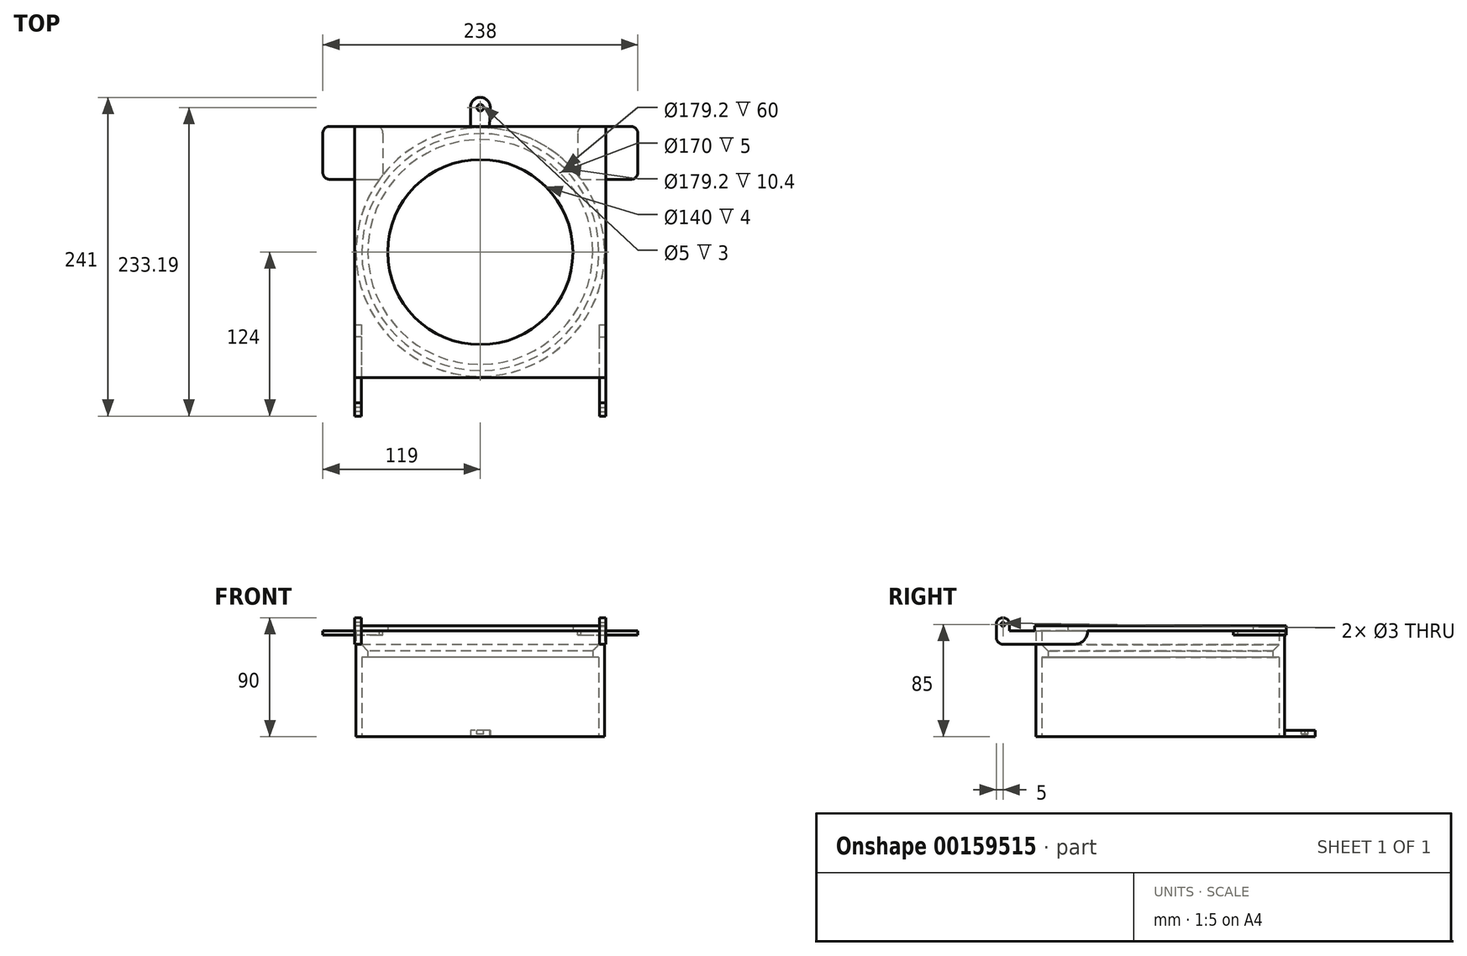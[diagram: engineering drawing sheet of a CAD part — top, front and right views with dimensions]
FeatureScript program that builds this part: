
annotation { "Feature Type Name" : "Feature", "Feature Type Description" : "" }
export const myFeature = defineFeature(function(context is Context, id is Id, definition is map)
    precondition{}
    {
        {
            var Q0;
            Q0=qCreatedBy(makeId("Top.planeOp"),FACE);
            var sketch = newSketch(context, id + "F0", { "sketchPlane" : qUnion([Q0])});
            skCircle(sketch, "E0", {"center": v(0, 0) * mm, "radius": 94 * mm});
            skCircle(sketch, "E1", {"center": v(0, 0) * mm, "radius": 89.6 * mm});
            skArc(sketch, "E2", {"start": v(7.5, 109.26) * mm, "mid": v(-0.04, 117) * mm, "end": v(-7.5, 109.19) * mm});
            skLineSegment(sketch, "E3", {"start": v(-7.5, 109.19) * mm, "end": v(-7.5, 93.7) * mm});
            skLineSegment(sketch, "E4", {"start": v(7.5, 109.26) * mm, "end": v(7, 93.74) * mm});
            skSolve(sketch);
        }
        {
            var Q0;
            Q0=makeQuery(id+"F0.imprint","IMPRINT",FACE,{"disambiguationData":[TD([[makeQuery(id+"F0.imprint","IMPRINT",EDGE,{"derivedFrom":sQuery(id+"F0.wireOp",EDGE,"E0")}),1.0]])]});
            extrude(context, id + "F1", {"entities" : qUnion([Q0]), "depth" : 60 * mm});
        }
        {
            var Q0;
            Q0=makeQuery(id+"F1.opExtrude","CAP_FACE",FACE,{"disambiguationData":[OSD([sQuery(id+"F0.wireOp",EDGE,"E0"),sQuery(id+"F0.wireOp",EDGE,"E1")])],"isStart":false});
            var sketch = newSketch(context, id + "F2", { "sketchPlane" : qUnion([Q0])});
            skCircle(sketch, "E5", {"center": v(0, 0) * mm, "radius": 94 * mm});
            skCircle(sketch, "E6", {"center": v(0, 0) * mm, "radius": 85 * mm});
            skSolve(sketch);
        }
        {
            var Q0;
            Q0=makeQuery(id+"F2.imprint","IMPRINT",FACE,{"disambiguationData":[TD([[makeQuery(id+"F2.imprint","IMPRINT",EDGE,{"derivedFrom":sQuery(id+"F2.wireOp",EDGE,"E6")}),-1.0]])]});
            var Q1;
            Q1=makeQuery(id+"F2.imprint","IMPRINT",FACE,{"disambiguationData":[TD([[makeQuery(id+"F2.imprint","IMPRINT",EDGE,{"derivedFrom":sQuery(id+"F2.wireOp",EDGE,"E5")}),1.0]])]});
            extrude(context, id + "F3", {"entities" : qUnion([Q0, Q1]), "operationType" : NewBodyOperationType.ADD, "depth" : 10 * mm});
        }
        {
            var Q0;
            Q0=makeQuery(id+"F3.opExtrude","CAP_FACE",FACE,{"disambiguationData":[OSD([sQuery(id+"F2.wireOp",EDGE,"E5"),sQuery(id+"F2.wireOp",EDGE,"E6")])],"isStart":false});
            var sketch = newSketch(context, id + "F4", { "sketchPlane" : qUnion([Q0])});
            skCircle(sketch, "E7", {"center": v(0, 0) * mm, "radius": 94 * mm});
            skCircle(sketch, "E8", {"center": v(0, 0) * mm, "radius": 89.6 * mm});
            skSolve(sketch);
        }
        {
            var Q0;
            Q0=makeQuery(id+"F4.imprint","IMPRINT",FACE,{"disambiguationData":[TD([[makeQuery(id+"F4.imprint","IMPRINT",EDGE,{"derivedFrom":sQuery(id+"F4.wireOp",EDGE,"E7")}),1.0]])]});
            extrude(context, id + "F5", {"entities" : qUnion([Q0]), "operationType" : NewBodyOperationType.ADD, "depth" : 10 * mm});
        }
        {
            var Q0;
            Q0=makeQuery(id+"F5.opExtrude","CAP_FACE",FACE,{"disambiguationData":[OSD([sQuery(id+"F4.wireOp",EDGE,"E7"),sQuery(id+"F4.wireOp",EDGE,"E8")])],"isStart":false});
            var sketch = newSketch(context, id + "F6", { "sketchPlane" : qUnion([Q0])});
            skLineSegment(sketch, "E9.bottom", {"start": v(95, -95) * mm, "end": v(-95, -95) * mm});
            skLineSegment(sketch, "E9.top", {"start": v(95, 95) * mm, "end": v(-95, 95) * mm});
            skLineSegment(sketch, "E9.left", {"start": v(95, -95) * mm, "end": v(95, 95) * mm});
            skLineSegment(sketch, "E9.right", {"start": v(-95, -95) * mm, "end": v(-95, 95) * mm});
            skPoint(sketch, "E9.middle", {"position": v(0, 0) * mm});
            skCircle(sketch, "E10", {"center": v(0, 0) * mm, "radius": 70 * mm});
            skSolve(sketch);
        }
        {
            var Q0;
            Q0=makeQuery(id+"F6.imprint","IMPRINT",FACE,{"disambiguationData":[TD([[makeQuery(id+"F6.imprint","IMPRINT",EDGE,{"derivedFrom":sQuery(id+"F6.wireOp",EDGE,"E9.bottom")}),-1.0]])]});
            var Q1;
            Q1=makeQuery(id+"F6.imprint","IMPRINT",FACE,{"disambiguationData":[TD([[makeQuery(id+"F6.imprint","IMPRINT",EDGE,{"derivedFrom":sQuery(id+"F6.wireOp",EDGE,"E10")}),-1.0]])]});
            var Q2;
            Q2=makeQuery(id+"F6.imprint","IMPRINT",FACE,{"disambiguationData":[TD([[makeQuery(id+"F6.imprint","IMPRINT",EDGE,{"derivedFrom":makeQuery(id+"F5.opExtrude","CAP_EDGE",EDGE,{"disambiguationData":[OSD([sQuery(id+"F4.wireOp",EDGE,"E7")])],"isStart":false})}),1.0]])]});
            extrude(context, id + "F7", {"entities" : qUnion([Q0, Q1, Q2]), "operationType" : NewBodyOperationType.ADD, "depth" : 4 * mm});
        }
        {
            var Q0;
            Q0=makeQuery(id+"F0.imprint","IMPRINT",FACE,{"disambiguationData":[TD([[makeQuery(id+"F0.imprint","IMPRINT",EDGE,{"derivedFrom":sQuery(id+"F0.wireOp",EDGE,"E2")}),1.0]])]});
            extrude(context, id + "F8", {"entities" : qUnion([Q0]), "operationType" : NewBodyOperationType.ADD, "depth" : 5 * mm});
        }
        {
            var Q0;
            Q0=makeQuery(id+"F8.opExtrude","CAP_FACE",FACE,{"disambiguationData":[OSD([sQuery(id+"F0.wireOp",EDGE,"E0"),sQuery(id+"F0.wireOp",EDGE,"E2"),sQuery(id+"F0.wireOp",EDGE,"E3"),sQuery(id+"F0.wireOp",EDGE,"E4")])],"isStart":false});
            var sketch = newSketch(context, id + "F9", { "sketchPlane" : qUnion([Q0])});
            skCircle(sketch, "E11", {"center": v(0, 109.19) * mm, "radius": 2.5 * mm});
            skSolve(sketch);
        }
        {
            var Q0;
            Q0=makeQuery(id+"F9.imprint","IMPRINT",FACE,{"disambiguationData":[TD([[makeQuery(id+"F9.imprint","IMPRINT",EDGE,{"derivedFrom":sQuery(id+"F9.wireOp",EDGE,"E11")}),1.0]])]});
            extrude(context, id + "F10", {"entities" : qUnion([Q0]), "operationType" : NewBodyOperationType.REMOVE, "oppositeDirection" : true, "depth" : 3 * mm});
        }
        {
            var Q0;
            Q0=makeQuery(id+"F3.opExtrude","CAP_EDGE",EDGE,{"disambiguationData":[OSD([sQuery(id+"F2.wireOp",EDGE,"E6")])],"isStart":false});
            chamfer(context, id + "F11", {"entities" : qUnion([Q0]), "width" : 5 * mm, "tangentPropagation" : true});
        }
        {
            var Q0;
            {var subQ0=sQuery(id+"F6.wireOp",EDGE,"E9.bottom");var subQ1=sQuery(id+"F6.wireOp",EDGE,"E9.top");var subQ2=sQuery(id+"F6.wireOp",EDGE,"E9.left");var subQ3=sQuery(id+"F6.wireOp",EDGE,"E9.right");Q0=makeQuery(id+"F7.boolean.opBoolean","SPLIT",FACE,{"disambiguationData":[TD([makeQuery(id+"F1.opExtrude","SWEPT_FACE",FACE,{"disambiguationData":[OSD([sQuery(id+"F0.wireOp",EDGE,"E0")])]})])],"derivedFrom":makeQuery(id+"F7.opExtrude","CAP_FACE",FACE,{"disambiguationData":[OSD([subQ0,subQ1,subQ2,subQ3,sQuery(id+"F6.wireOp",EDGE,"E10")])],"isStart":true})});}
            var sketch = newSketch(context, id + "F12", { "sketchPlane" : qUnion([Q0])});
            skLineSegment(sketch, "E12.bottom", {"start": v(95, -95) * mm, "end": v(114, -95) * mm});
            skLineSegment(sketch, "E12.top", {"start": v(95, -55) * mm, "end": v(114, -55) * mm});
            skLineSegment(sketch, "E12.right", {"start": v(119, -90) * mm, "end": v(119, -60) * mm});
            skPoint(sketch, "E13.visualSharp", {"position": v(119, -95) * mm});
            skArc(sketch, "E13.filletArc", {"start": v(114, -95) * mm, "mid": v(117.54, -93.54) * mm, "end": v(119, -90) * mm});
            skPoint(sketch, "E14.visualSharp", {"position": v(119, -55) * mm});
            skArc(sketch, "E14.filletArc", {"start": v(119, -60) * mm, "mid": v(117.54, -56.46) * mm, "end": v(114, -55) * mm});
            skLineSegment(sketch, "E15.bottom", {"start": v(95, -95) * mm, "end": v(78.59, -95) * mm});
            skLineSegment(sketch, "E15.top", {"start": v(95, -55) * mm, "end": v(73.59, -55) * mm});
            skLineSegment(sketch, "E15.right", {"start": v(73.59, -90) * mm, "end": v(73.59, -55) * mm});
            skPoint(sketch, "E16.visualSharp", {"position": v(73.59, -95) * mm});
            skArc(sketch, "E16.filletArc", {"start": v(73.59, -90) * mm, "mid": v(75.05, -93.54) * mm, "end": v(78.59, -95) * mm});
            skLineSegment(sketch, "E17.MirrorCS", {"start": v(-95, -95) * mm, "end": v(-114, -95) * mm});
            skLineSegment(sketch, "E18.MirrorCS", {"start": v(-95, -95) * mm, "end": v(-78.59, -95) * mm});
            skArc(sketch, "E19.MirrorCS", {"start": v(-73.59, -90) * mm, "mid": v(-75.05, -93.54) * mm, "end": v(-78.59, -95) * mm});
            skLineSegment(sketch, "E20.MirrorCS", {"start": v(-73.59, -90) * mm, "end": v(-73.59, -55) * mm});
            skLineSegment(sketch, "E21.MirrorCS", {"start": v(-95, -55) * mm, "end": v(-73.59, -55) * mm});
            skLineSegment(sketch, "E22.MirrorCS", {"start": v(-95, -55) * mm, "end": v(-114, -55) * mm});
            skArc(sketch, "E23.MirrorCS", {"start": v(-119, -60) * mm, "mid": v(-117.54, -56.46) * mm, "end": v(-114, -55) * mm});
            skLineSegment(sketch, "E24.MirrorCS", {"start": v(-119, -90) * mm, "end": v(-119, -60) * mm});
            skArc(sketch, "E25.MirrorCS", {"start": v(-114, -95) * mm, "mid": v(-117.54, -93.54) * mm, "end": v(-119, -90) * mm});
            skSolve(sketch);
        }
        {
            var Q0;
            {var subQ1=sQuery(id+"F12.wireOp",EDGE,"E12.bottom");Q0=makeQuery(id+"F12.imprint","IMPRINT",FACE,{"disambiguationData":[TD([[makeQuery(id+"F12.imprint","IMPRINT",EDGE,{"derivedFrom":subQ1}),1.0]])]});}
            var Q1;
            {var subQ8=sQuery(id+"F12.wireOp",EDGE,"E15.bottom");Q1=makeQuery(id+"F12.imprint","IMPRINT",FACE,{"disambiguationData":[TD([[makeQuery(id+"F12.imprint","IMPRINT",EDGE,{"derivedFrom":subQ8}),-1.0]])]});}
            var Q2;
            {var subQ8=sQuery(id+"F12.wireOp",EDGE,"E18.MirrorCS");Q2=makeQuery(id+"F12.imprint","IMPRINT",FACE,{"disambiguationData":[TD([[makeQuery(id+"F12.imprint","IMPRINT",EDGE,{"derivedFrom":subQ8}),-1.0]])]});}
            var Q3;
            {var subQ1=sQuery(id+"F12.wireOp",EDGE,"E17.MirrorCS");Q3=makeQuery(id+"F12.imprint","IMPRINT",FACE,{"disambiguationData":[TD([[makeQuery(id+"F12.imprint","IMPRINT",EDGE,{"derivedFrom":subQ1}),-1.0]])]});}
            extrude(context, id + "F13", {"entities" : qUnion([Q0, Q1, Q2, Q3]), "operationType" : NewBodyOperationType.ADD, "depth" : 3 * mm});
        }
        {
            var Q0;
            {var subQ0=sQuery(id+"F6.wireOp",EDGE,"E9.bottom");var subQ1=makeQuery(id+"F7.opExtrude","SWEPT_FACE",FACE,{"disambiguationData":[OSD([subQ0])]});var subQ9=makeQuery(id+"F1.opExtrude","SWEPT_FACE",FACE,{"disambiguationData":[OSD([sQuery(id+"F0.wireOp",EDGE,"E0")])]});var subQ10=sQuery(id+"F6.wireOp",EDGE,"E9.left");var subQ12=sQuery(id+"F6.wireOp",EDGE,"E9.right");var subQ14=sQuery(id+"F6.wireOp",EDGE,"E9.top");Q0=makeQuery(id+"F13.boolean.opBoolean","SPLIT",FACE,{"disambiguationData":[TD([subQ1])],"derivedFrom":makeQuery(id+"F7.boolean.opBoolean","SPLIT",FACE,{"disambiguationData":[TD([subQ9])],"derivedFrom":makeQuery(id+"F7.opExtrude","CAP_FACE",FACE,{"disambiguationData":[OSD([subQ0,subQ14,subQ10,subQ12,sQuery(id+"F6.wireOp",EDGE,"E10")])],"isStart":true})})});}
            var sketch = newSketch(context, id + "F14", { "sketchPlane" : qUnion([Q0])});
            skLineSegment(sketch, "E26.bottom", {"start": v(-95, 95) * mm, "end": v(-90, 95) * mm});
            skLineSegment(sketch, "E26.top", {"start": v(-95, 119) * mm, "end": v(-90, 119) * mm});
            skLineSegment(sketch, "E26.left", {"start": v(-95, 95) * mm, "end": v(-95, 119) * mm});
            skLineSegment(sketch, "E26.right", {"start": v(-90, 95) * mm, "end": v(-90, 119) * mm});
            skLineSegment(sketch, "E27.top", {"start": v(-95, 55) * mm, "end": v(-90, 55) * mm});
            skLineSegment(sketch, "E27.left", {"start": v(-95, 95) * mm, "end": v(-95, 55) * mm});
            skLineSegment(sketch, "E27.right", {"start": v(-90, 95) * mm, "end": v(-90, 55) * mm});
            skLineSegment(sketch, "E28.top", {"start": v(-95, 124) * mm, "end": v(-90, 124) * mm});
            skLineSegment(sketch, "E28.left", {"start": v(-95, 119) * mm, "end": v(-95, 124) * mm});
            skLineSegment(sketch, "E28.right", {"start": v(-90, 119) * mm, "end": v(-90, 124) * mm});
            skSolve(sketch);
        }
        {
            var Q0;
            Q0 = qSketchRegion(id + "F14", true);
            extrude(context, id + "F15", {"entities" : qUnion([Q0]), "operationType" : NewBodyOperationType.ADD, "depth" : 10 * mm});
        }
        {
            var Q0;
            Q0=makeQuery(id+"F15.boolean.opBoolean","MERGE",FACE,{"derivedFrom":[makeQuery(id+"F7.opExtrude","SWEPT_FACE",FACE,{"disambiguationData":[OSD([sQuery(id+"F6.wireOp",EDGE,"E9.right")])]}),makeQuery(id+"F15.opExtrude","SWEPT_FACE",FACE,{"disambiguationData":[OSD([sQuery(id+"F14.wireOp",EDGE,"E26.left"),sQuery(id+"F14.wireOp",EDGE,"E27.left")])]})]});
            var sketch = newSketch(context, id + "F16", { "sketchPlane" : qUnion([Q0])});
            skArc(sketch, "E29", {"start": v(55, 80) * mm, "mid": v(58.27, 72.58) * mm, "end": v(65.95, 70) * mm});
            skSolve(sketch);
        }
        {
            var Q0;
            Q0 = qSketchRegion(id + "F16", true);
            var Q1;
            {var subQ3=sQuery(id+"F6.wireOp",EDGE,"E9.right");var subQ5=sQuery(id+"F14.wireOp",EDGE,"E27.left");var subQ6=makeQuery(id+"F15.opExtrude","SWEPT_EDGE",EDGE,{"disambiguationData":[OSD([subQ3,sQuery(id+"F14.wireOp",EDGE,"E27.top"),subQ5])]});Q1=makeQuery(id+"F16.imprint","IMPRINT",FACE,{"disambiguationData":[TD([[makeQuery(id+"F16.imprint","IMPRINT",EDGE,{"derivedFrom":subQ6}),-1.0]])]});}
            extrude(context, id + "F17", {"entities" : qUnion([Q0, Q1]), "operationType" : NewBodyOperationType.REMOVE, "endBound" : BoundingType.UP_TO_NEXT, "oppositeDirection" : true, "depth" : 25 * mm});
        }
        {
            var Q0;
            Q0=makeQuery(id+"F15.opExtrude","CAP_EDGE",EDGE,{"disambiguationData":[OSD([sQuery(id+"F14.wireOp",EDGE,"E28.top")])],"isStart":false});
            fillet(context, id + "F18", {"entities" : qUnion([Q0]), "radius" : 5 * mm, "tangentPropagation" : true, "allowEdgeOverflow" : false});
        }
        {
            var Q0;
            Q0=makeQuery(id+"F15.boolean.opBoolean","MERGE",FACE,{"derivedFrom":[makeQuery(id+"F7.opExtrude","SWEPT_FACE",FACE,{"disambiguationData":[OSD([sQuery(id+"F6.wireOp",EDGE,"E9.right")])]}),makeQuery(id+"F15.opExtrude","SWEPT_FACE",FACE,{"disambiguationData":[OSD([sQuery(id+"F14.wireOp",EDGE,"E26.left"),sQuery(id+"F14.wireOp",EDGE,"E27.left"),sQuery(id+"F14.wireOp",EDGE,"E28.left")])]})]});
            var sketch = newSketch(context, id + "F19", { "sketchPlane" : qUnion([Q0])});
            skLineSegment(sketch, "E30.bottom", {"start": v(124, 80) * mm, "end": v(114, 80) * mm});
            skLineSegment(sketch, "E30.top", {"start": v(119, 90) * mm, "end": v(119, 90) * mm});
            skLineSegment(sketch, "E30.left", {"start": v(124, 80) * mm, "end": v(124, 85) * mm});
            skLineSegment(sketch, "E30.right", {"start": v(114, 80) * mm, "end": v(114, 85) * mm});
            skPoint(sketch, "E31.visualSharp", {"position": v(124, 90) * mm});
            skArc(sketch, "E31.filletArc", {"start": v(124, 85) * mm, "mid": v(122.54, 88.54) * mm, "end": v(119, 90) * mm});
            skPoint(sketch, "E32.visualSharp", {"position": v(114, 90) * mm});
            skArc(sketch, "E32.filletArc", {"start": v(119, 90) * mm, "mid": v(115.46, 88.54) * mm, "end": v(114, 85) * mm});
            skSolve(sketch);
        }
        {
            var Q0;
            Q0=makeQuery(id+"F19.imprint","IMPRINT",FACE,{"disambiguationData":[TD([[makeQuery(id+"F19.imprint","IMPRINT",EDGE,{"derivedFrom":sQuery(id+"F19.wireOp",EDGE,"E30.bottom")}),1.0]])]});
            extrude(context, id + "F20", {"entities" : qUnion([Q0]), "operationType" : NewBodyOperationType.ADD, "oppositeDirection" : true, "depth" : 5 * mm});
        }
        {
            var Q0;
            Q0=makeQuery(id+"F20.boolean.opBoolean","MERGE",FACE,{"derivedFrom":[makeQuery(id+"F15.boolean.opBoolean","MERGE",FACE,{"derivedFrom":[makeQuery(id+"F7.opExtrude","SWEPT_FACE",FACE,{"disambiguationData":[OSD([sQuery(id+"F6.wireOp",EDGE,"E9.right")])]}),makeQuery(id+"F15.opExtrude","SWEPT_FACE",FACE,{"disambiguationData":[OSD([sQuery(id+"F14.wireOp",EDGE,"E26.left"),sQuery(id+"F14.wireOp",EDGE,"E27.left"),sQuery(id+"F14.wireOp",EDGE,"E28.left")])]})]}),makeQuery(id+"F20.opExtrude","CAP_FACE",FACE,{"disambiguationData":[OSD([sQuery(id+"F19.wireOp",EDGE,"E30.bottom"),sQuery(id+"F19.wireOp",EDGE,"E30.left"),sQuery(id+"F19.wireOp",EDGE,"E30.right"),sQuery(id+"F19.wireOp",EDGE,"E31.filletArc"),sQuery(id+"F19.wireOp",EDGE,"E32.filletArc")])],"isStart":true})]});
            var sketch = newSketch(context, id + "F21", { "sketchPlane" : qUnion([Q0])});
            skCircle(sketch, "E33", {"center": v(119, 85) * mm, "radius": 1.5 * mm});
            skSolve(sketch);
        }
        {
            var Q0;
            Q0=makeQuery(id+"F21.imprint","IMPRINT",FACE,{"disambiguationData":[TD([[makeQuery(id+"F21.imprint","IMPRINT",EDGE,{"derivedFrom":sQuery(id+"F21.wireOp",EDGE,"E33")}),1.0]])]});
            extrude(context, id + "F22", {"entities" : qUnion([Q0]), "operationType" : NewBodyOperationType.REMOVE, "endBound" : BoundingType.UP_TO_NEXT, "oppositeDirection" : true, "depth" : 25 * mm});
        }
        {
            var Q0;
            Q0=makeQuery(id+"F7.opExtrude","SWEPT_FACE",FACE,{"disambiguationData":[OSD([sQuery(id+"F6.wireOp",EDGE,"E9.left")])]});
            var sketch = newSketch(context, id + "F23", { "sketchPlane" : qUnion([Q0])});
            skLineSegment(sketch, "E34.0.0", {"start": v(-124, 85) * mm, "end": v(-124, 75) * mm});
            skArc(sketch, "E34.0.1", {"start": v(-124, 75) * mm, "mid": v(-122.54, 71.46) * mm, "end": v(-119, 70) * mm});
            skLineSegment(sketch, "E34.0.2", {"start": v(-119, 70) * mm, "end": v(-64.13, 70) * mm});
            skArc(sketch, "E34.0.3", {"start": v(-64.13, 70) * mm, "mid": v(-57.63, 73.23) * mm, "end": v(-55, 80) * mm});
            skLineSegment(sketch, "E34.0.4", {"start": v(-55, 80) * mm, "end": v(-95, 80) * mm});
            skLineSegment(sketch, "E34.0.5", {"start": v(-95, 80) * mm, "end": v(-114, 80) * mm});
            skLineSegment(sketch, "E34.0.6", {"start": v(-114, 80) * mm, "end": v(-114, 85) * mm});
            skArc(sketch, "E34.0.7", {"start": v(-114, 85) * mm, "mid": v(-119, 90) * mm, "end": v(-124, 85) * mm});
            skCircle(sketch, "E35.0", {"center": v(-119, 85) * mm, "radius": 1.5 * mm});
            skSolve(sketch);
        }
        {
            var Q0;
            Q0=makeQuery(id+"F23.imprint","IMPRINT",FACE,{"disambiguationData":[TD([[makeQuery(id+"F23.imprint","IMPRINT",EDGE,{"derivedFrom":sQuery(id+"F23.wireOp",EDGE,"E34.0.0")}),1.0]])]});
            extrude(context, id + "F24", {"entities" : qUnion([Q0]), "operationType" : NewBodyOperationType.ADD, "oppositeDirection" : true, "depth" : 5 * mm});
        }
    });
